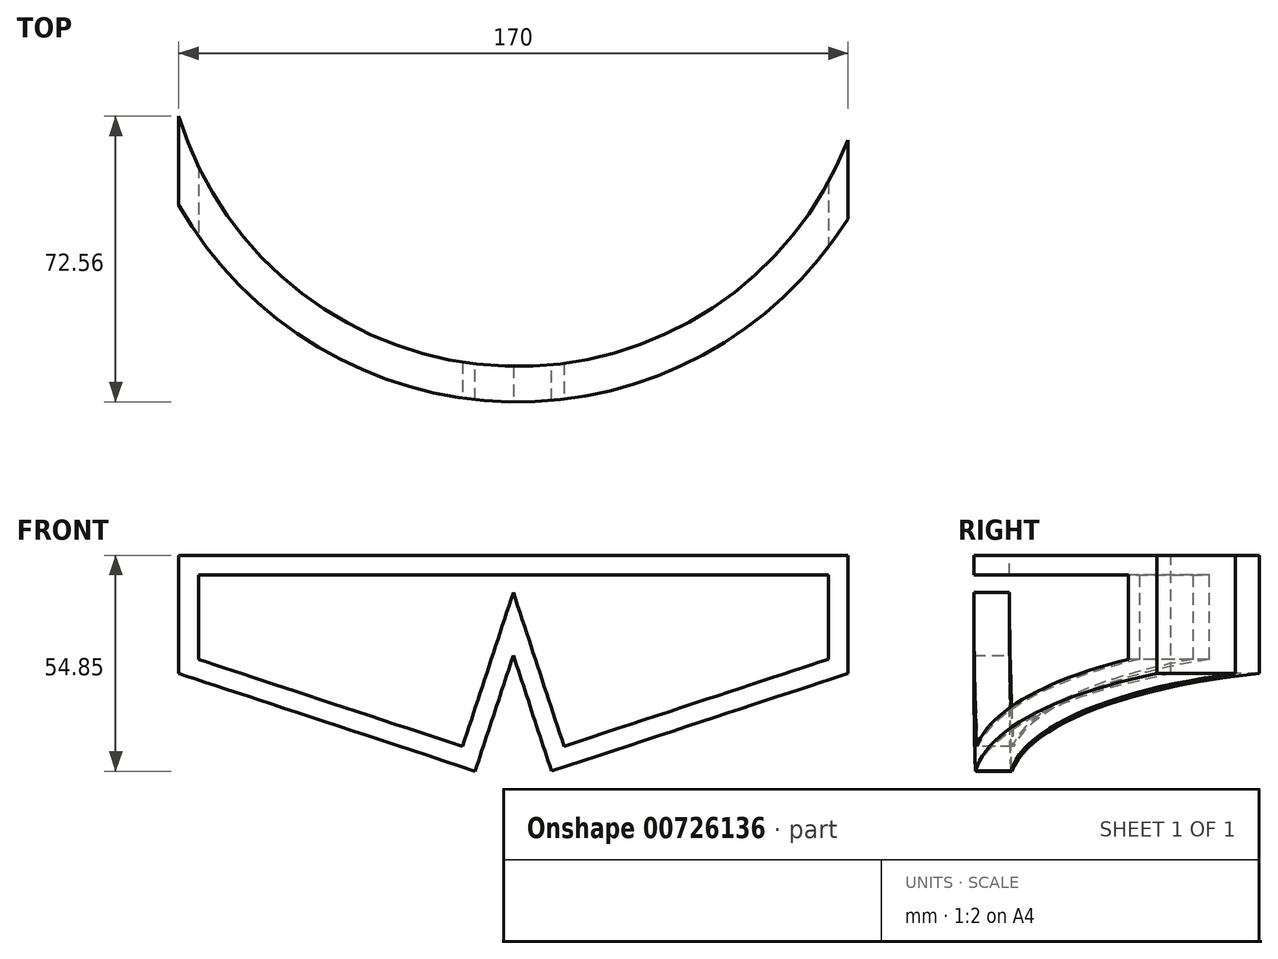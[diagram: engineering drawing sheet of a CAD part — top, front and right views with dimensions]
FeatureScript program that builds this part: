
annotation { "Feature Type Name" : "Feature", "Feature Type Description" : "" }
export const myFeature = defineFeature(function(context is Context, id is Id, definition is map)
    precondition{}
    {
        {
            var Q0;
            Q0=qCreatedBy(makeId("Front.planeOp"),FACE);
            var sketch = newSketch(context, id + "F0", { "sketchPlane" : qUnion([Q0])});
            skLineSegment(sketch, "E0.top", {"start": v(-20.04, 65.04) * mm, "end": v(-105.04, 65.04) * mm});
            skLineSegment(sketch, "E1", {"start": v(-29.75, 10.2) * mm, "end": v(-20.04, 39.64) * mm});
            skLineSegment(sketch, "E2", {"start": v(-29.75, 10.2) * mm, "end": v(-105.04, 35.02) * mm});
            skLineSegment(sketch, "E3", {"start": v(-105.04, 65.04) * mm, "end": v(-105.04, 35.02) * mm});
            skLineSegment(sketch, "E4.MirrorCS", {"start": v(64.96, 65.04) * mm, "end": v(64.96, 35.04) * mm});
            skLineSegment(sketch, "E5.MirrorCS", {"start": v(-10.34, 10.24) * mm, "end": v(64.96, 35.04) * mm});
            skLineSegment(sketch, "E6.MirrorCS", {"start": v(-20.04, 65.04) * mm, "end": v(64.96, 65.04) * mm});
            skLineSegment(sketch, "E7.MirrorCS", {"start": v(-10.34, 10.24) * mm, "end": v(-20.04, 39.64) * mm});
            skSolve(sketch);
        }
        {
            var Q0;
            Q0=makeQuery(id+"F0.imprint","IMPRINT",FACE,{"disambiguationData":[TD([[makeQuery(id+"F0.imprint","IMPRINT",EDGE,{"derivedFrom":sQuery(id+"F0.wireOp",EDGE,"E0.top")}),1.0]])]});
            extrude(context, id + "F1", {"entities" : qUnion([Q0]), "endBound" : BoundingType.SYMMETRIC, "depth" : 150 * mm, "offsetDistance" : 25 * mm});
        }
        {
            var Q0;
            Q0=makeQuery(id+"F1.opExtrude","CAP_FACE",FACE,{"disambiguationData":[OSD([sQuery(id+"F0.wireOp",EDGE,"E0.top"),sQuery(id+"F0.wireOp",EDGE,"E1"),sQuery(id+"F0.wireOp",EDGE,"E2"),sQuery(id+"F0.wireOp",EDGE,"E3"),sQuery(id+"F0.wireOp",EDGE,"E4.MirrorCS"),sQuery(id+"F0.wireOp",EDGE,"E5.MirrorCS"),sQuery(id+"F0.wireOp",EDGE,"E6.MirrorCS"),sQuery(id+"F0.wireOp",EDGE,"E7.MirrorCS")])],"isStart":false});
            var sketch = newSketch(context, id + "F2", { "sketchPlane" : qUnion([Q0])});
            skLineSegment(sketch, "E8.0", {"start": v(-32.93, 16.5) * mm, "end": v(-20.04, 55.6) * mm});
            skLineSegment(sketch, "E8.1", {"start": v(-7.16, 16.55) * mm, "end": v(-20.04, 55.6) * mm});
            skLineSegment(sketch, "E8.2", {"start": v(-100.04, 60.04) * mm, "end": v(-100.04, 38.64) * mm});
            skLineSegment(sketch, "E8.3", {"start": v(-100.04, 60.04) * mm, "end": v(59.96, 60.04) * mm});
            skLineSegment(sketch, "E8.4", {"start": v(59.96, 60.04) * mm, "end": v(59.96, 38.66) * mm});
            skLineSegment(sketch, "E8.5", {"start": v(-32.93, 16.5) * mm, "end": v(-100.04, 38.64) * mm});
            skLineSegment(sketch, "E8.6", {"start": v(-7.16, 16.55) * mm, "end": v(59.96, 38.66) * mm});
            skSolve(sketch);
        }
        {
            var Q0;
            Q0=makeQuery(id+"F1.opExtrude","SWEPT_FACE",FACE,{"disambiguationData":[OSD([sQuery(id+"F0.wireOp",EDGE,"E0.top"),sQuery(id+"F0.wireOp",EDGE,"E6.MirrorCS")])]});
            var sketch = newSketch(context, id + "F3", { "sketchPlane" : qUnion([Q0])});
            skArc(sketch, "E9", {"start": v(-116, 40.66) * mm, "mid": v(-18.98, -38.45) * mm, "end": v(78.03, 40.66) * mm});
            skArc(sketch, "E10.0", {"start": v(-107.18, 42.47) * mm, "mid": v(-18.98, -29.45) * mm, "end": v(69.22, 42.47) * mm});
            skLineSegment(sketch, "E11", {"start": v(-116, 40.66) * mm, "end": v(-107.18, 42.47) * mm});
            skLineSegment(sketch, "E12", {"start": v(69.22, 42.47) * mm, "end": v(78.03, 40.66) * mm});
            skSolve(sketch);
        }
        {
            var Q0;
            Q0 = qSketchRegion(id + "F2", true);
            extrude(context, id + "F4", {"entities" : qUnion([Q0]), "operationType" : NewBodyOperationType.REMOVE, "oppositeDirection" : true, "depth" : 200 * mm, "offsetDistance" : 25 * mm});
        }
        {
            var Q0;
            Q0 = qSketchRegion(id + "F3", true);
            extrude(context, id + "F5", {"entities" : qUnion([Q0]), "operationType" : NewBodyOperationType.INTERSECT, "oppositeDirection" : true, "depth" : 100 * mm, "offsetDistance" : 25 * mm});
        }
    });
